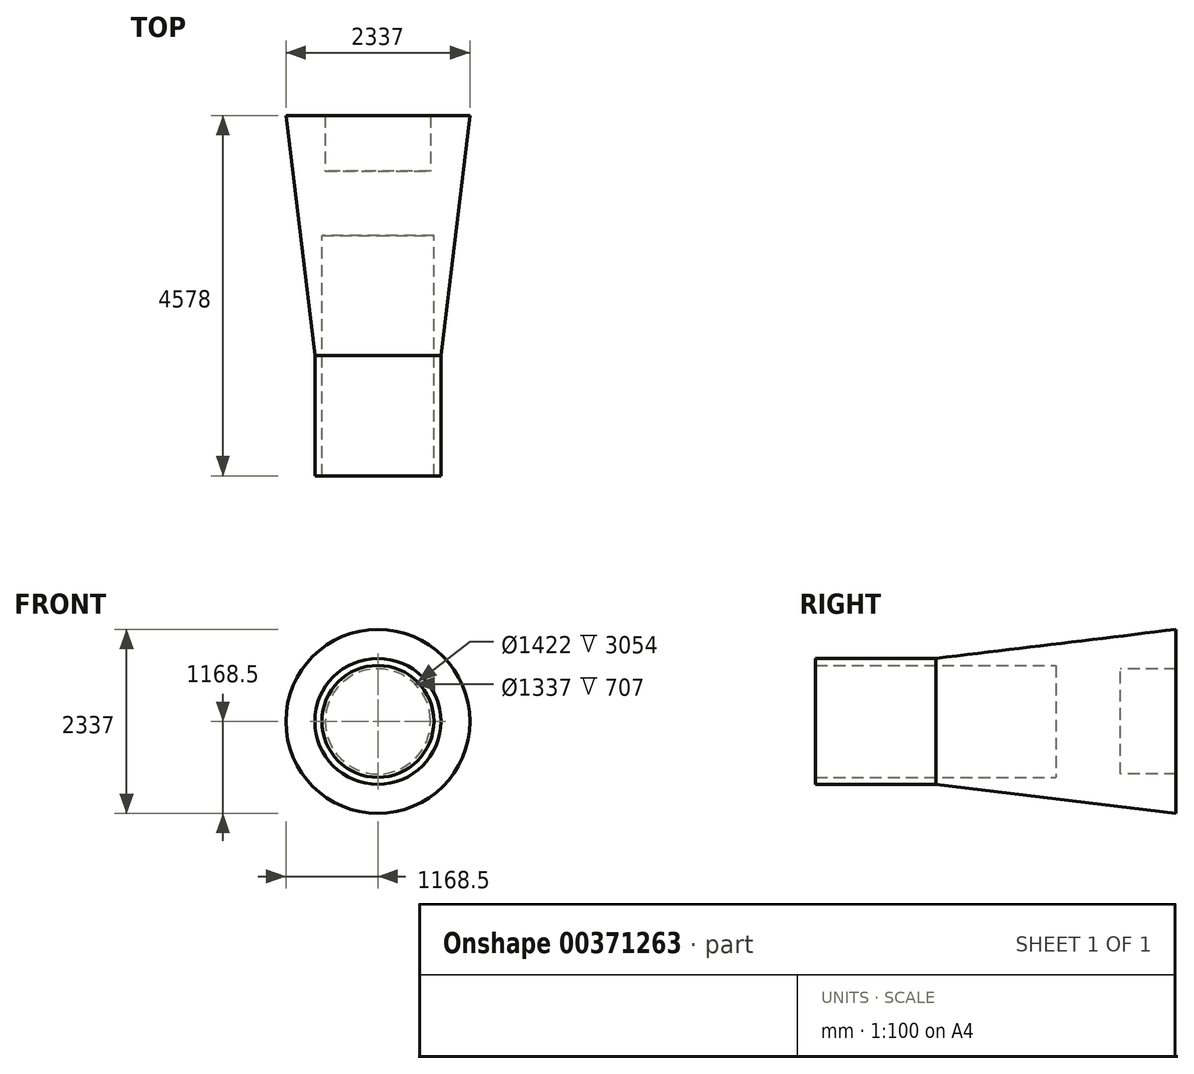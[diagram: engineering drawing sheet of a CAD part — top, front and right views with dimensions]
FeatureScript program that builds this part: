
annotation { "Feature Type Name" : "Feature", "Feature Type Description" : "" }
export const myFeature = defineFeature(function(context is Context, id is Id, definition is map)
    precondition{}
    {
        {
            var Q0;
            Q0=qCreatedBy(makeId("Right.planeOp"),FACE);
            var sketch = newSketch(context, id + "F0", { "sketchPlane" : qUnion([Q0])});
            skLineSegment(sketch, "E0", {"start": v(0, 0) * mm, "end": v(-3048, 0) * mm});
            skLineSegment(sketch, "E1", {"start": v(-3048, 800) * mm, "end": v(0, 1168.5) * mm});
            skLineSegment(sketch, "E2", {"start": v(0, 0) * mm, "end": v(0, 1168.5) * mm});
            skLineSegment(sketch, "E3", {"start": v(-3048, 0) * mm, "end": v(-4578, 0) * mm});
            skLineSegment(sketch, "E4", {"start": v(-4578, 0) * mm, "end": v(-4578, 800) * mm});
            skLineSegment(sketch, "E5", {"start": v(-4578, 800) * mm, "end": v(-3048, 800) * mm});
            skSolve(sketch);
        }
        {
            var Q0;
            Q0=makeQuery(id+"F0.imprint","IMPRINT",FACE,{"disambiguationData":[TD([[makeQuery(id+"F0.imprint","IMPRINT",EDGE,{"derivedFrom":sQuery(id+"F0.wireOp",EDGE,"E0")}),-1.0]])]});
            var sketch = newSketch(context, id + "F1", { "sketchPlane" : qUnion([Q0])});
            skLineSegment(sketch, "E6", {"start": v(-3048, 0) * mm, "end": v(-1524, 0) * mm});
            skLineSegment(sketch, "E7", {"start": v(-1524, 0) * mm, "end": v(-1524, 711) * mm});
            skLineSegment(sketch, "E8", {"start": v(-1524, 711) * mm, "end": v(-3048, 711) * mm});
            skLineSegment(sketch, "E9", {"start": v(0, 0) * mm, "end": v(0, 1369) * mm, "construction": true});
            skLineSegment(sketch, "E10", {"start": v(-3048, 0) * mm, "end": v(0, 0) * mm, "construction": true});
            skLineSegment(sketch, "E11", {"start": v(-3048, 0) * mm, "end": v(-4810.84, 0) * mm});
            skLineSegment(sketch, "E12", {"start": v(-4816.08, 711) * mm, "end": v(-3048, 711) * mm});
            skLineSegment(sketch, "E13", {"start": v(-4816.08, 711) * mm, "end": v(-4810.84, 0) * mm});
            skSolve(sketch);
        }
        {
            var Q0;
            Q0=qCreatedBy(makeId("Right.planeOp"),FACE);
            var sketch = newSketch(context, id + "F2", { "sketchPlane" : qUnion([Q0])});
            skLineSegment(sketch, "E14.bottom", {"start": v(0, 0) * mm, "end": v(-707, 0) * mm});
            skLineSegment(sketch, "E14.top", {"start": v(0, 668.5) * mm, "end": v(-707, 668.5) * mm});
            skLineSegment(sketch, "E14.left", {"start": v(0, 0) * mm, "end": v(0, 668.5) * mm});
            skLineSegment(sketch, "E14.right", {"start": v(-707, 0) * mm, "end": v(-707, 668.5) * mm});
            skSolve(sketch);
        }
        {
            var Q0;
            Q0 = qSketchRegion(id + "F0", true);
            var Q1;
            Q1=sQuery(id+"F0.wireOp",EDGE,"E0");
            revolve(context, id + "F3", {"entities" : qUnion([Q0]), "axis" : qUnion([Q1]), "revolveType" : RevolveType.FULL});
        }
        {
            var Q0;
            Q0 = qSketchRegion(id + "F1", true);
            var Q1;
            Q1=sQuery(id+"F1.wireOp",EDGE,"E6");
            revolve(context, id + "F4", {"operationType" : NewBodyOperationType.REMOVE, "entities" : qUnion([Q0]), "axis" : qUnion([Q1]), "revolveType" : RevolveType.FULL, "oppositeDirection" : true});
        }
        {
            var Q0;
            Q0 = qSketchRegion(id + "F2", true);
            var Q1;
            Q1=sQuery(id+"F2.wireOp",EDGE,"E14.bottom");
            revolve(context, id + "F5", {"operationType" : NewBodyOperationType.REMOVE, "entities" : qUnion([Q0]), "axis" : qUnion([Q1]), "revolveType" : RevolveType.FULL, "oppositeDirection" : true});
        }
    });
